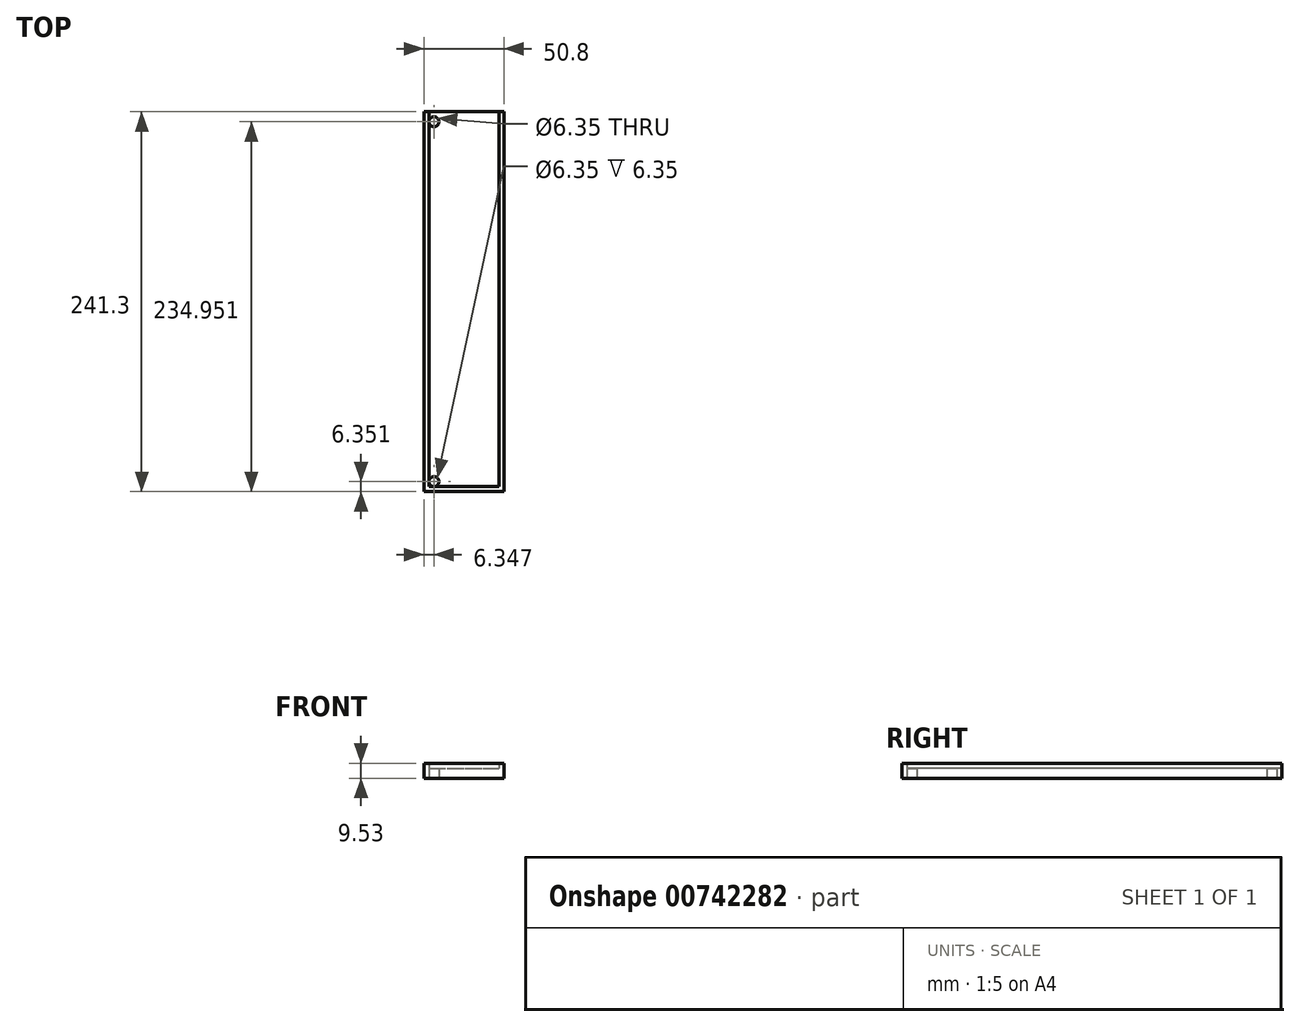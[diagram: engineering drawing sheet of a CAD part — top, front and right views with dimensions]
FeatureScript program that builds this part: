
annotation { "Feature Type Name" : "Feature", "Feature Type Description" : "" }
export const myFeature = defineFeature(function(context is Context, id is Id, definition is map)
    precondition{}
    {
        {
            var Q0;
            Q0=qCreatedBy(makeId("Top.planeOp"),FACE);
            var sketch = newSketch(context, id + "F0", { "sketchPlane" : qUnion([Q0])});
            skLineSegment(sketch, "E0.bottom", {"start": v(-46.87, 171.3) * mm, "end": v(3.93, 171.3) * mm});
            skLineSegment(sketch, "E0.top", {"start": v(-46.87, -70) * mm, "end": v(3.93, -70) * mm});
            skLineSegment(sketch, "E0.left", {"start": v(-46.87, 171.3) * mm, "end": v(-46.87, -70) * mm});
            skLineSegment(sketch, "E0.right", {"start": v(3.93, 171.3) * mm, "end": v(3.93, -70) * mm});
            skLineSegment(sketch, "E1.bottom", {"start": v(-46.87, 171.3) * mm, "end": v(-43.7, 171.3) * mm});
            skLineSegment(sketch, "E1.left", {"start": v(-46.87, 171.3) * mm, "end": v(-46.87, 168.12) * mm});
            skLineSegment(sketch, "E1.right", {"start": v(-43.7, 171.3) * mm, "end": v(-43.7, 168.12) * mm});
            skLineSegment(sketch, "E2.bottom", {"start": v(3.93, 171.3) * mm, "end": v(0.75, 171.3) * mm});
            skLineSegment(sketch, "E2.left", {"start": v(3.93, 171.3) * mm, "end": v(3.93, 168.12) * mm});
            skLineSegment(sketch, "E2.right", {"start": v(0.75, 171.3) * mm, "end": v(0.75, 168.12) * mm});
            skLineSegment(sketch, "E3.bottom", {"start": v(-46.87, -70) * mm, "end": v(-43.7, -70) * mm});
            skLineSegment(sketch, "E3.left", {"start": v(-46.87, -70) * mm, "end": v(-46.87, -66.83) * mm});
            skLineSegment(sketch, "E4.bottom", {"start": v(3.93, -70) * mm, "end": v(0.75, -70) * mm});
            skLineSegment(sketch, "E4.left", {"start": v(3.93, -70) * mm, "end": v(3.93, -66.83) * mm});
            skLineSegment(sketch, "E5.right", {"start": v(0.75, 168.12) * mm, "end": v(0.75, -66.83) * mm});
            skLineSegment(sketch, "E6.bottom", {"start": v(-46.87, -70) * mm, "end": v(-34.17, -70) * mm});
            skLineSegment(sketch, "E6.left", {"start": v(-46.87, -70) * mm, "end": v(-46.87, -57.3) * mm});
            skLineSegment(sketch, "E7.bottom", {"start": v(-46.87, 171.3) * mm, "end": v(-34.17, 171.3) * mm});
            skLineSegment(sketch, "E7.left", {"start": v(-46.87, 171.3) * mm, "end": v(-46.87, 158.6) * mm});
            skLineSegment(sketch, "E8", {"start": v(-43.7, -66.83) * mm, "end": v(-46.87, -66.83) * mm});
            skCircle(sketch, "E9", {"center": v(-40.52, 164.94) * mm, "radius": 3.18 * mm});
            skCircle(sketch, "E10", {"center": v(-40.52, -63.66) * mm, "radius": 3.18 * mm});
            skLineSegment(sketch, "E11", {"start": v(-40.52, 168.12) * mm, "end": v(0.75, 168.12) * mm});
            skLineSegment(sketch, "E12", {"start": v(-43.7, 168.12) * mm, "end": v(-46.87, 168.12) * mm});
            skLineSegment(sketch, "E13", {"start": v(0.75, 168.12) * mm, "end": v(3.93, 168.12) * mm});
            skLineSegment(sketch, "E14", {"start": v(-40.52, -66.83) * mm, "end": v(0.75, -66.83) * mm});
            skLineSegment(sketch, "E15", {"start": v(0.75, -66.83) * mm, "end": v(0.75, -70) * mm});
            skLineSegment(sketch, "E16", {"start": v(0.75, -66.83) * mm, "end": v(3.93, -66.83) * mm});
            skLineSegment(sketch, "E17", {"start": v(-43.7, 164.94) * mm, "end": v(-43.7, -63.66) * mm});
            skLineSegment(sketch, "E18", {"start": v(-43.7, -66.83) * mm, "end": v(-43.7, -70) * mm});
            skLineSegment(sketch, "E19", {"start": v(-43.7, 164.94) * mm, "end": v(-43.7, 168.12) * mm});
            skLineSegment(sketch, "E20", {"start": v(-43.7, -66.83) * mm, "end": v(-43.7, -63.66) * mm});
            skLineSegment(sketch, "E21", {"start": v(-43.7, -66.83) * mm, "end": v(-40.52, -66.83) * mm});
            skLineSegment(sketch, "E22", {"start": v(-40.52, 168.12) * mm, "end": v(-43.7, 168.12) * mm});
            skSolve(sketch);
        }
        {
            var Q0;
            {var subQ0=sQuery(id+"F0.wireOp",EDGE,"E1.right");Q0=makeQuery(id+"F0.imprint","IMPRINT",FACE,{"disambiguationData":[TD([[makeQuery(id+"F0.imprint","IMPRINT",EDGE,{"derivedFrom":subQ0}),-1.0]])]});}
            var Q1;
            {var subQ1=sQuery(id+"F0.wireOp",EDGE,"E0.left");Q1=makeQuery(id+"F0.imprint","IMPRINT",FACE,{"disambiguationData":[TD([[makeQuery(id+"F0.imprint","IMPRINT",EDGE,{"derivedFrom":subQ1}),1.0]])]});}
            var Q2;
            Q2=makeQuery(id+"F0.imprint","IMPRINT",FACE,{"disambiguationData":[TD([[makeQuery(id+"F0.imprint","IMPRINT",EDGE,{"derivedFrom":sQuery(id+"F0.wireOp",EDGE,"E2.bottom")}),1.0]])]});
            var Q3;
            Q3=makeQuery(id+"F0.imprint","IMPRINT",FACE,{"disambiguationData":[TD([[makeQuery(id+"F0.imprint","IMPRINT",EDGE,{"derivedFrom":sQuery(id+"F0.wireOp",EDGE,"E0.right")}),-1.0]])]});
            var Q4;
            {var subQ4=sQuery(id+"F0.wireOp",EDGE,"E8");Q4=makeQuery(id+"F0.imprint","IMPRINT",FACE,{"disambiguationData":[TD([[makeQuery(id+"F0.imprint","IMPRINT",EDGE,{"derivedFrom":subQ4}),1.0]])]});}
            var Q5;
            {var subQ1=sQuery(id+"F0.wireOp",EDGE,"E0.top");Q5=makeQuery(id+"F0.imprint","IMPRINT",FACE,{"disambiguationData":[TD([[makeQuery(id+"F0.imprint","IMPRINT",EDGE,{"derivedFrom":subQ1}),1.0]])]});}
            var Q6;
            Q6=makeQuery(id+"F0.imprint","IMPRINT",FACE,{"disambiguationData":[TD([[makeQuery(id+"F0.imprint","IMPRINT",EDGE,{"derivedFrom":sQuery(id+"F0.wireOp",EDGE,"E4.bottom")}),-1.0]])]});
            extrude(context, id + "F1", {"entities" : qUnion([Q0, Q1, Q2, Q3, Q4, Q5, Q6]), "depth" : 9.52 * mm, "offsetDistance" : 25.4 * mm});
        }
        {
            var Q0;
            Q0=makeQuery(id+"F0.imprint","IMPRINT",FACE,{"disambiguationData":[TD([[makeQuery(id+"F0.imprint","IMPRINT",EDGE,{"derivedFrom":sQuery(id+"F0.wireOp",EDGE,"E5.right")}),-1.0]])]});
            var Q1;
            {var subQ1=sQuery(id+"F0.wireOp",EDGE,"E0.bottom");Q1=makeQuery(id+"F0.imprint","IMPRINT",FACE,{"disambiguationData":[TD([[makeQuery(id+"F0.imprint","IMPRINT",EDGE,{"derivedFrom":subQ1}),-1.0]])]});}
            extrude(context, id + "F2", {"entities" : qUnion([Q0, Q1]), "operationType" : NewBodyOperationType.ADD, "depth" : 6.35 * mm, "offsetDistance" : 25.4 * mm});
        }
        {
            var Q0;
            {var subQ2=sQuery(id+"F0.wireOp",EDGE,"E19");Q0=makeQuery(id+"F0.imprint","IMPRINT",FACE,{"disambiguationData":[TD([[makeQuery(id+"F0.imprint","IMPRINT",EDGE,{"derivedFrom":subQ2}),-1.0]])]});}
            var Q1;
            {var subQ2=sQuery(id+"F0.wireOp",EDGE,"E20");Q1=makeQuery(id+"F0.imprint","IMPRINT",FACE,{"disambiguationData":[TD([[makeQuery(id+"F0.imprint","IMPRINT",EDGE,{"derivedFrom":subQ2}),-1.0]])]});}
            extrude(context, id + "F3", {"entities" : qUnion([Q0, Q1]), "operationType" : NewBodyOperationType.ADD, "depth" : 6.35 * mm, "offsetDistance" : 25.4 * mm});
        }
    });
